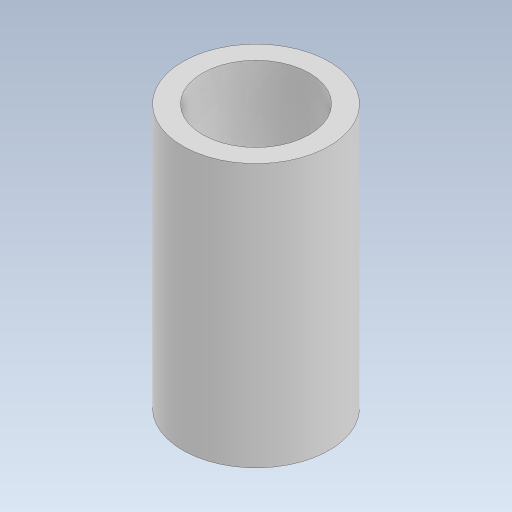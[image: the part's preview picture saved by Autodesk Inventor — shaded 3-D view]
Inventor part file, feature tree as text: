
AUTODESK INVENTOR PART (.ipt)
format: ipt  version: 2023.5 (Build 275446000, 446)  size: 90,624 bytes
history: native  units: mm
features: extrude x1, sketch x1
ambient origin geometry x8: Origin, YZ Plane, XZ Plane, XY Plane, X Axis, Y Axis, Z Axis, Center Point
bodies: Solid1 (feature_tree)
feature tree (2):
  extrude  "Extrusion1"  Depth=10.0mm
  sketch  "Sketch1"  dims[d0=7.3mm d1=10.0mm d2=18.0mm d3=0.0mm]
